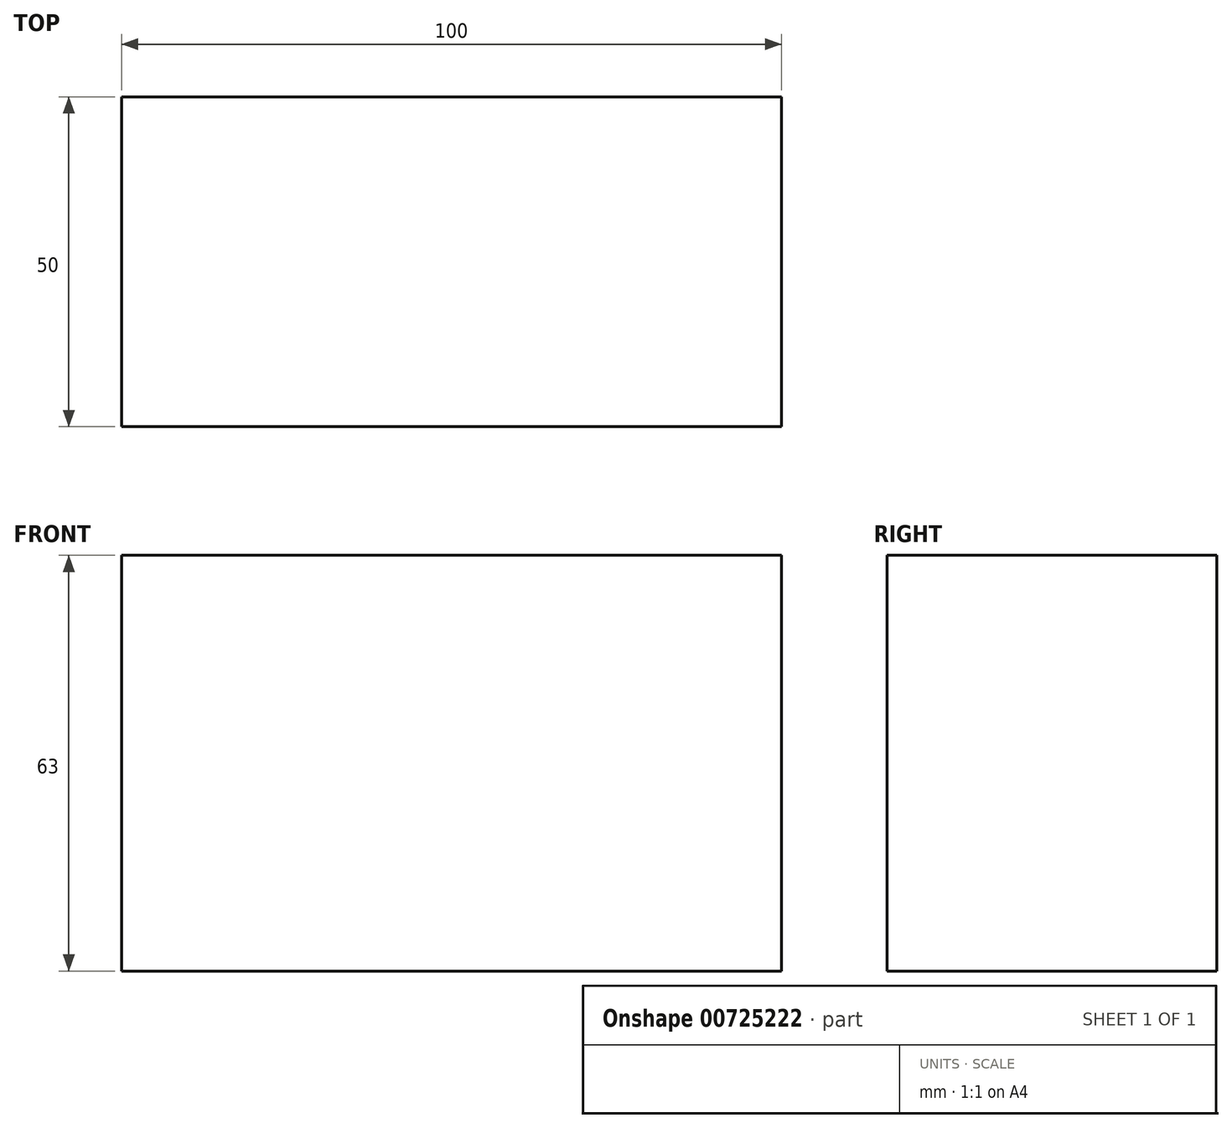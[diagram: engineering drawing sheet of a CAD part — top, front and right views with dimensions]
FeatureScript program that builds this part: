
annotation { "Feature Type Name" : "Feature", "Feature Type Description" : "" }
export const myFeature = defineFeature(function(context is Context, id is Id, definition is map)
    precondition{}
    {
        {
            assignVariable(context, id + "F0", {"name" : "B", "anyValue" : 50 * mm});
        }
        {
            var Q0;
            Q0=qCreatedBy(makeId("Front.planeOp"),FACE);
            var sketch = newSketch(context, id + "F1", { "sketchPlane" : qUnion([Q0])});
            skLineSegment(sketch, "E0", {"start": v(0, 0) * mm, "end": v(100, 0) * mm});
            skLineSegment(sketch, "E1", {"start": v(100, 0) * mm, "end": v(100, 63) * mm});
            skLineSegment(sketch, "E2", {"start": v(100, 63) * mm, "end": v(0, 63) * mm});
            skLineSegment(sketch, "E3", {"start": v(0, 63) * mm, "end": v(0, 0) * mm});
            skSolve(sketch);
        }
        {
            var Q0;
            Q0 = qSketchRegion(id + "F1", true);
            extrude(context, id + "F2", {"entities" : qUnion([Q0]), "depth" : getVariable(context, 'B'), "offsetDistance" : 25.4 * mm});
        }
    });
